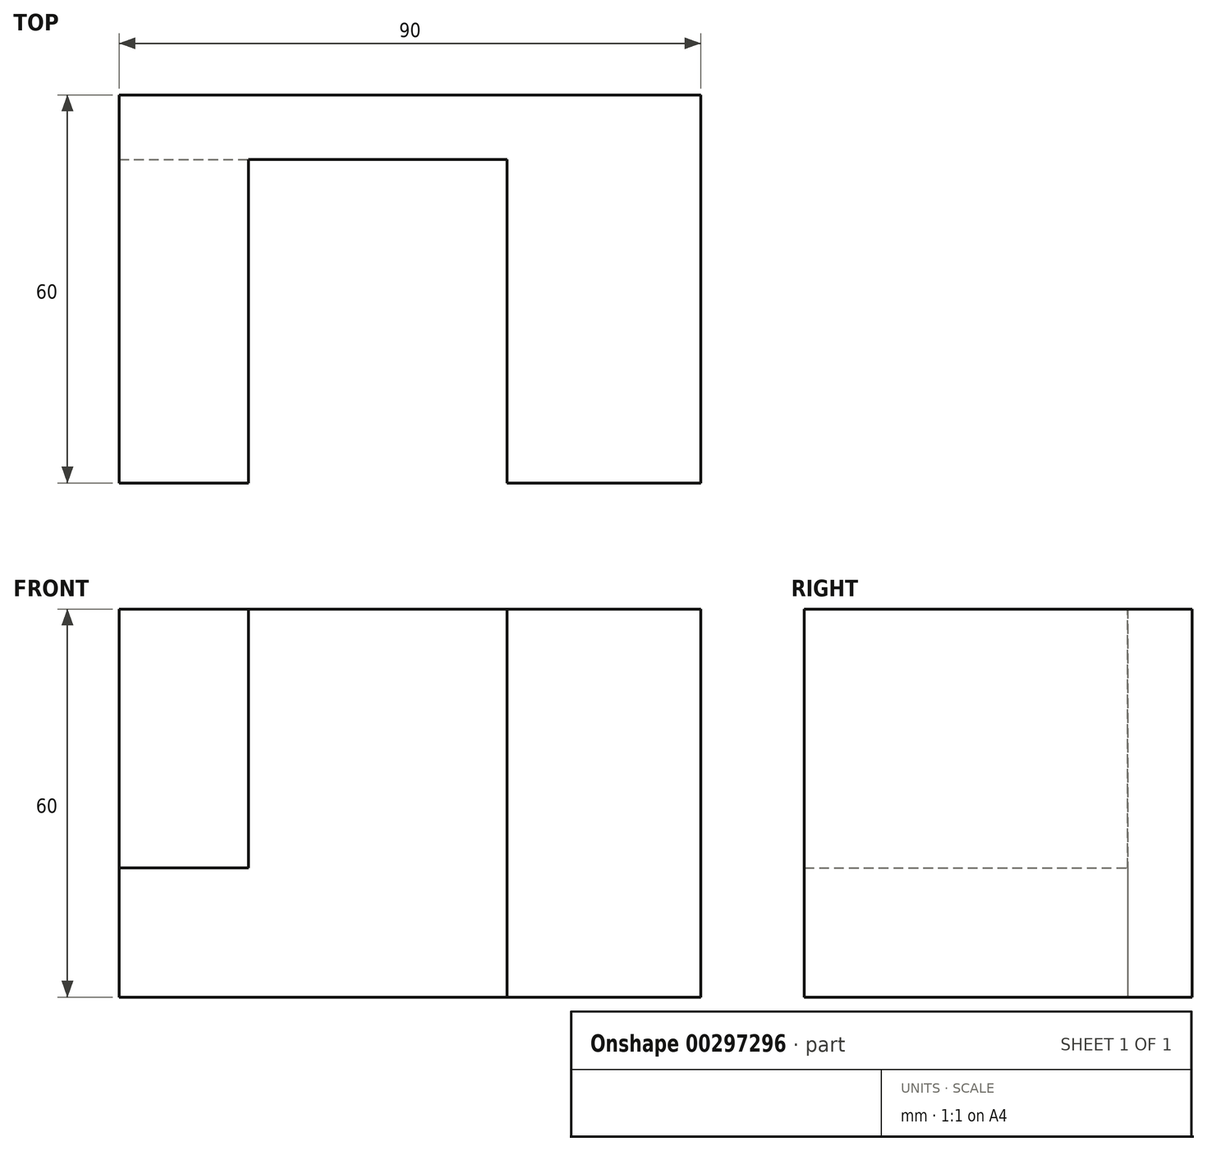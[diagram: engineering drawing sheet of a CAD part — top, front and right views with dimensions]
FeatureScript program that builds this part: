
annotation { "Feature Type Name" : "Feature", "Feature Type Description" : "" }
export const myFeature = defineFeature(function(context is Context, id is Id, definition is map)
    precondition{}
    {
        {
            var Q0;
            Q0=qCreatedBy(makeId("Front.planeOp"),FACE);
            var sketch = newSketch(context, id + "F0", { "sketchPlane" : qUnion([Q0])});
            skLineSegment(sketch, "E0.bottom", {"start": v(-45.3, 32.97) * mm, "end": v(44.7, 32.97) * mm});
            skLineSegment(sketch, "E0.top", {"start": v(-45.3, -27.03) * mm, "end": v(44.7, -27.03) * mm});
            skLineSegment(sketch, "E0.left", {"start": v(-45.3, 32.97) * mm, "end": v(-45.3, -27.03) * mm});
            skLineSegment(sketch, "E0.right", {"start": v(44.7, 32.97) * mm, "end": v(44.7, -27.03) * mm});
            skLineSegment(sketch, "E1.bottom", {"start": v(-45.3, -7.03) * mm, "end": v(-25.3, -7.03) * mm});
            skLineSegment(sketch, "E1.top", {"start": v(-45.3, 32.97) * mm, "end": v(-25.3, 32.97) * mm});
            skLineSegment(sketch, "E1.left", {"start": v(-45.3, -7.03) * mm, "end": v(-45.3, 32.97) * mm});
            skLineSegment(sketch, "E1.right", {"start": v(-25.3, -7.03) * mm, "end": v(-25.3, 32.97) * mm});
            skLineSegment(sketch, "E2.bottom", {"start": v(-35.3, -27.03) * mm, "end": v(4.7, -27.03) * mm});
            skLineSegment(sketch, "E2.top", {"start": v(-35.3, -17.03) * mm, "end": v(4.7, -17.03) * mm});
            skLineSegment(sketch, "E2.left", {"start": v(-35.3, -27.03) * mm, "end": v(-35.3, -17.03) * mm});
            skLineSegment(sketch, "E2.right", {"start": v(4.7, -27.03) * mm, "end": v(4.7, -17.03) * mm});
            skLineSegment(sketch, "E3.bottom", {"start": v(14.7, 32.97) * mm, "end": v(44.7, 32.97) * mm});
            skLineSegment(sketch, "E3.top", {"start": v(14.7, -27.03) * mm, "end": v(44.7, -27.03) * mm});
            skLineSegment(sketch, "E3.left", {"start": v(14.7, 32.97) * mm, "end": v(14.7, -27.03) * mm});
            skSolve(sketch);
        }
        {
            var Q0;
            Q0=makeQuery(id+"F0.imprint","IMPRINT",FACE,{"disambiguationData":[TD([[makeQuery(id+"F0.imprint","IMPRINT",EDGE,{"derivedFrom":sQuery(id+"F0.wireOp",EDGE,"E0.bottom")}),-1.0]])]});
            extrude(context, id + "F1", {"entities" : qUnion([Q0]), "depth" : 60 * mm});
        }
        {
            var Q0;
            Q0 = qSketchRegion(id + "F0", true);
            extrude(context, id + "F2", {"entities" : qUnion([Q0]), "operationType" : NewBodyOperationType.ADD, "depth" : 10 * mm});
        }
        {
            var Q0;
            Q0=makeQuery(id+"F0.imprint","IMPRINT",FACE,{"disambiguationData":[TD([[makeQuery(id+"F0.imprint","IMPRINT",EDGE,{"derivedFrom":sQuery(id+"F0.wireOp",EDGE,"E1.bottom")}),1.0]])]});
            extrude(context, id + "F3", {"entities" : qUnion([Q0]), "operationType" : NewBodyOperationType.ADD, "depth" : 30 * mm});
        }
    });
